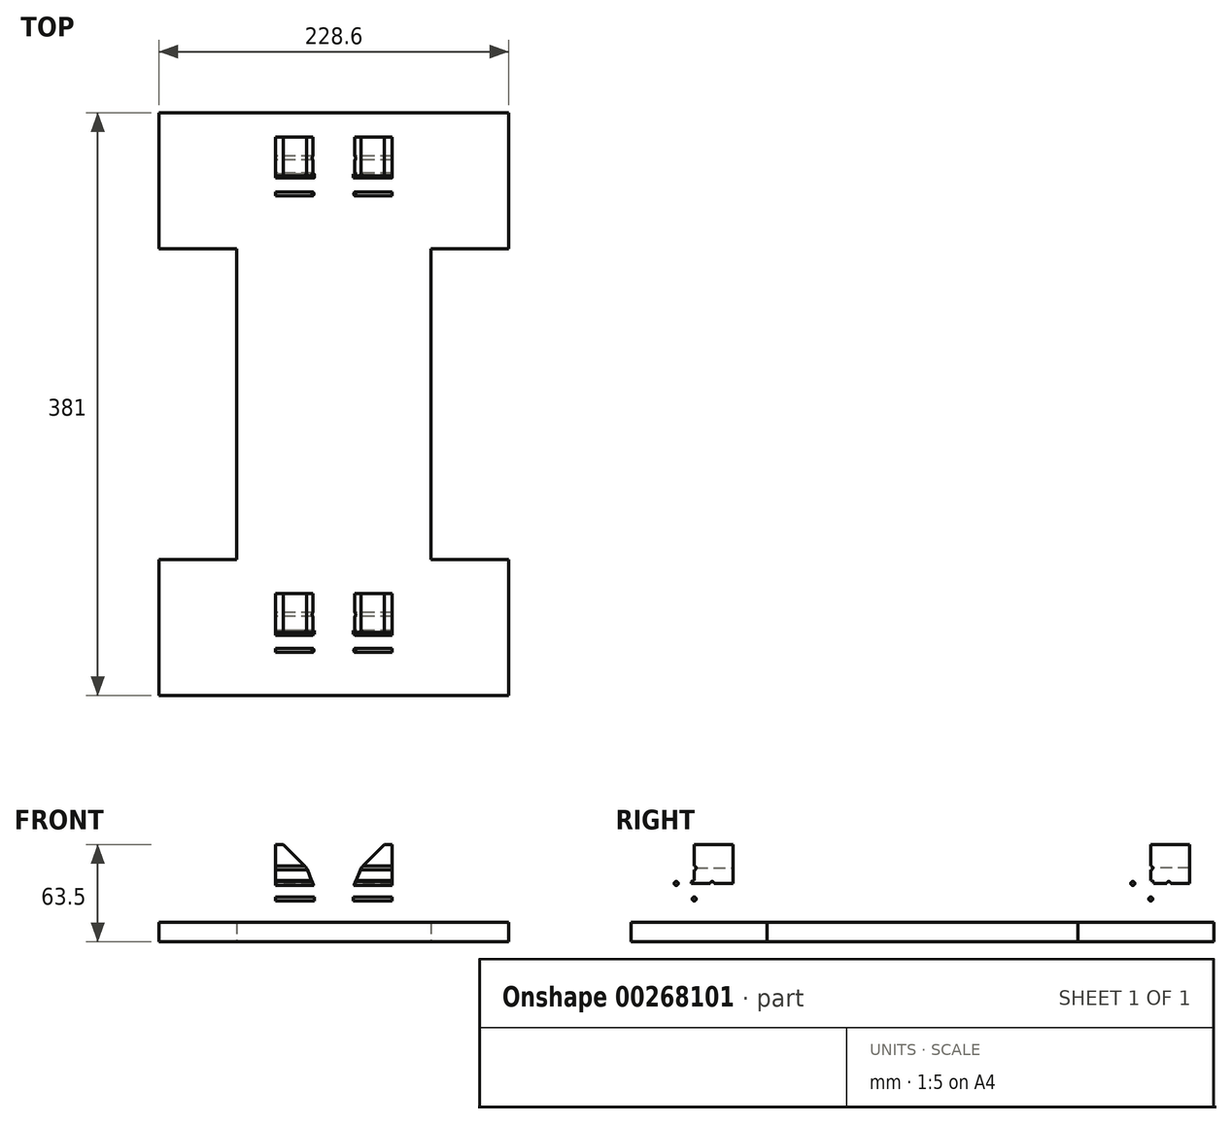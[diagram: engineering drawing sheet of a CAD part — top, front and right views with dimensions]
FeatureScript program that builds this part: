
annotation { "Feature Type Name" : "Feature", "Feature Type Description" : "" }
export const myFeature = defineFeature(function(context is Context, id is Id, definition is map)
    precondition{}
    {
        {
            var Q0;
            Q0=qCreatedBy(makeId("Top.planeOp"),FACE);
            var sketch = newSketch(context, id + "F0", { "sketchPlane" : qUnion([Q0])});
            skLineSegment(sketch, "E0.bottom", {"start": v(0, 0) * mm, "end": v(228.6, 0) * mm});
            skLineSegment(sketch, "E0.top", {"start": v(0, 381) * mm, "end": v(228.6, 381) * mm});
            skLineSegment(sketch, "E0.left", {"start": v(0, 0) * mm, "end": v(0, 381) * mm});
            skLineSegment(sketch, "E0.right", {"start": v(228.6, 0) * mm, "end": v(228.6, 381) * mm});
            skLineSegment(sketch, "E1", {"start": v(114.3, 381) * mm, "end": v(114.3, 0) * mm});
            skLineSegment(sketch, "E2", {"start": v(0, 190.5) * mm, "end": v(228.6, 190.5) * mm});
            skLineSegment(sketch, "E3.bottom", {"start": v(0, 190.5) * mm, "end": v(50.8, 190.5) * mm});
            skLineSegment(sketch, "E3.top", {"start": v(0, 88.9) * mm, "end": v(50.8, 88.9) * mm});
            skLineSegment(sketch, "E3.left", {"start": v(0, 190.5) * mm, "end": v(0, 88.9) * mm});
            skLineSegment(sketch, "E3.right", {"start": v(50.8, 190.5) * mm, "end": v(50.8, 88.9) * mm});
            skLineSegment(sketch, "E4.MirrorCS", {"start": v(50.8, 190.5) * mm, "end": v(50.8, 292.1) * mm});
            skLineSegment(sketch, "E5.MirrorCS", {"start": v(0, 292.1) * mm, "end": v(50.8, 292.1) * mm});
            skLineSegment(sketch, "E6.MirrorCS", {"start": v(177.8, 190.5) * mm, "end": v(177.8, 292.1) * mm});
            skLineSegment(sketch, "E7.MirrorCS", {"start": v(177.8, 190.5) * mm, "end": v(177.8, 88.9) * mm});
            skLineSegment(sketch, "E8.MirrorCS", {"start": v(228.6, 292.1) * mm, "end": v(177.8, 292.1) * mm});
            skLineSegment(sketch, "E9.MirrorCS", {"start": v(228.6, 88.9) * mm, "end": v(177.8, 88.9) * mm});
            skSolve(sketch);
        }
        {
            var Q0;
            {var subQ0=sQuery(id+"F0.wireOp",EDGE,"E4.MirrorCS");Q0=makeQuery(id+"F0.imprint","IMPRINT",FACE,{"disambiguationData":[TD([[makeQuery(id+"F0.imprint","IMPRINT",EDGE,{"derivedFrom":subQ0}),-1.0]])]});}
            var Q1;
            {var subQ0=sQuery(id+"F0.wireOp",EDGE,"E6.MirrorCS");Q1=makeQuery(id+"F0.imprint","IMPRINT",FACE,{"disambiguationData":[TD([[makeQuery(id+"F0.imprint","IMPRINT",EDGE,{"derivedFrom":subQ0}),1.0]])]});}
            var Q2;
            {var subQ4=sQuery(id+"F0.wireOp",EDGE,"E3.top");Q2=makeQuery(id+"F0.imprint","IMPRINT",FACE,{"disambiguationData":[TD([[makeQuery(id+"F0.imprint","IMPRINT",EDGE,{"derivedFrom":subQ4}),-1.0]])]});}
            var Q3;
            {var subQ0=sQuery(id+"F0.wireOp",EDGE,"E7.MirrorCS");Q3=makeQuery(id+"F0.imprint","IMPRINT",FACE,{"disambiguationData":[TD([[makeQuery(id+"F0.imprint","IMPRINT",EDGE,{"derivedFrom":subQ0}),-1.0]])]});}
            extrude(context, id + "F1", {"entities" : qUnion([Q0, Q1, Q2, Q3]), "depth" : 12.7 * mm});
        }
        {
            var Q0;
            Q0=qCreatedBy(makeId("Top.planeOp"),FACE);
            var sketch = newSketch(context, id + "F2", { "sketchPlane" : qUnion([Q0])});
            skLineSegment(sketch, "E10", {"start": v(0, 0) * mm, "end": v(0, 397.67) * mm});
            skLineSegment(sketch, "E11", {"start": v(0, 0) * mm, "end": v(531.22, 0) * mm});
            skLineSegment(sketch, "E12.bottom", {"start": v(76.2, 15.88) * mm, "end": v(101.6, 15.88) * mm});
            skLineSegment(sketch, "E12.top", {"start": v(76.2, 66.68) * mm, "end": v(101.6, 66.68) * mm});
            skLineSegment(sketch, "E12.left", {"start": v(76.2, 15.88) * mm, "end": v(76.2, 66.68) * mm});
            skLineSegment(sketch, "E12.right", {"start": v(101.6, 15.88) * mm, "end": v(101.6, 66.68) * mm});
            skLineSegment(sketch, "E13", {"start": v(0, 190.5) * mm, "end": v(186.8, 190.5) * mm});
            skLineSegment(sketch, "E14", {"start": v(114.3, 0) * mm, "end": v(114.3, 473.13) * mm});
            skLineSegment(sketch, "E15.MirrorCS", {"start": v(127, 15.88) * mm, "end": v(127, 66.68) * mm});
            skLineSegment(sketch, "E16.MirrorCS", {"start": v(152.4, 66.68) * mm, "end": v(127, 66.68) * mm});
            skLineSegment(sketch, "E17.MirrorCS", {"start": v(152.4, 15.88) * mm, "end": v(152.4, 66.68) * mm});
            skLineSegment(sketch, "E18.MirrorCS", {"start": v(152.4, 15.88) * mm, "end": v(127, 15.88) * mm});
            skLineSegment(sketch, "E19.MirrorCS", {"start": v(76.2, 314.33) * mm, "end": v(101.6, 314.33) * mm});
            skLineSegment(sketch, "E20.MirrorCS", {"start": v(76.2, 365.13) * mm, "end": v(76.2, 314.33) * mm});
            skLineSegment(sketch, "E21.MirrorCS", {"start": v(101.6, 365.13) * mm, "end": v(101.6, 314.33) * mm});
            skLineSegment(sketch, "E22.MirrorCS", {"start": v(76.2, 365.13) * mm, "end": v(101.6, 365.13) * mm});
            skLineSegment(sketch, "E23.MirrorCS", {"start": v(152.4, 314.33) * mm, "end": v(127, 314.33) * mm});
            skLineSegment(sketch, "E24.MirrorCS", {"start": v(127, 365.13) * mm, "end": v(127, 314.33) * mm});
            skLineSegment(sketch, "E25.MirrorCS", {"start": v(152.4, 365.13) * mm, "end": v(152.4, 314.33) * mm});
            skLineSegment(sketch, "E26.MirrorCS", {"start": v(152.4, 365.13) * mm, "end": v(127, 365.13) * mm});
            skSolve(sketch);
        }
        {
            var Q0;
            Q0=makeQuery(id+"F2.imprint","IMPRINT",FACE,{"disambiguationData":[TD([[makeQuery(id+"F2.imprint","IMPRINT",EDGE,{"derivedFrom":sQuery(id+"F2.wireOp",EDGE,"E23.MirrorCS")}),-1.0]])]});
            var Q1;
            Q1=makeQuery(id+"F2.imprint","IMPRINT",FACE,{"disambiguationData":[TD([[makeQuery(id+"F2.imprint","IMPRINT",EDGE,{"derivedFrom":sQuery(id+"F2.wireOp",EDGE,"E19.MirrorCS")}),1.0]])]});
            var Q2;
            Q2=makeQuery(id+"F2.imprint","IMPRINT",FACE,{"disambiguationData":[TD([[makeQuery(id+"F2.imprint","IMPRINT",EDGE,{"derivedFrom":sQuery(id+"F2.wireOp",EDGE,"E15.MirrorCS")}),-1.0]])]});
            var Q3;
            Q3=makeQuery(id+"F2.imprint","IMPRINT",FACE,{"disambiguationData":[TD([[makeQuery(id+"F2.imprint","IMPRINT",EDGE,{"derivedFrom":sQuery(id+"F2.wireOp",EDGE,"E12.bottom")}),1.0]])]});
            extrude(context, id + "F3", {"entities" : qUnion([Q0, Q1, Q2, Q3]), "operationType" : NewBodyOperationType.ADD, "depth" : 63.5 * mm});
        }
        {
            var Q0;
            Q0=makeQuery(id+"F3.opExtrude","CAP_EDGE",EDGE,{"disambiguationData":[OSD([sQuery(id+"F2.wireOp",EDGE,"E12.right")])],"isStart":false});
            var Q1;
            Q1=makeQuery(id+"F3.opExtrude","CAP_EDGE",EDGE,{"disambiguationData":[OSD([sQuery(id+"F2.wireOp",EDGE,"E15.MirrorCS")])],"isStart":false});
            var Q2;
            Q2=makeQuery(id+"F3.opExtrude","CAP_EDGE",EDGE,{"disambiguationData":[OSD([sQuery(id+"F2.wireOp",EDGE,"E24.MirrorCS")])],"isStart":false});
            var Q3;
            Q3=makeQuery(id+"F3.opExtrude","CAP_EDGE",EDGE,{"disambiguationData":[OSD([sQuery(id+"F2.wireOp",EDGE,"E21.MirrorCS")])],"isStart":false});
            chamfer(context, id + "F4", {"entities" : qUnion([Q0, Q1, Q2, Q3]), "width" : 20.32 * mm, "tangentPropagation" : true});
        }
        {
            var Q0;
            {var subQ0=sQuery(id+"F2.wireOp",EDGE,"E24.MirrorCS");Q0=makeQuery(id+"F4.opChamfer","BLEND_EDGE",EDGE,{"blendedFrom":[makeQuery(id+"F3.opExtrude","CAP_EDGE",EDGE,{"disambiguationData":[OSD([subQ0])],"isStart":false}),makeQuery(id+"F3.opExtrude","SWEPT_FACE",FACE,{"disambiguationData":[OSD([subQ0])]})],"blendedInto":[makeQuery(id+"F3.opExtrude","SWEPT_FACE",FACE,{"disambiguationData":[OSD([subQ0])]})]});}
            var Q1;
            {var subQ0=sQuery(id+"F2.wireOp",EDGE,"E21.MirrorCS");Q1=makeQuery(id+"F4.opChamfer","BLEND_EDGE",EDGE,{"blendedFrom":[makeQuery(id+"F3.opExtrude","CAP_EDGE",EDGE,{"disambiguationData":[OSD([subQ0])],"isStart":false}),makeQuery(id+"F3.opExtrude","SWEPT_FACE",FACE,{"disambiguationData":[OSD([subQ0])]})],"blendedInto":[makeQuery(id+"F3.opExtrude","SWEPT_FACE",FACE,{"disambiguationData":[OSD([subQ0])]})]});}
            var Q2;
            {var subQ0=sQuery(id+"F2.wireOp",EDGE,"E15.MirrorCS");Q2=makeQuery(id+"F4.opChamfer","BLEND_EDGE",EDGE,{"blendedFrom":[makeQuery(id+"F3.opExtrude","CAP_EDGE",EDGE,{"disambiguationData":[OSD([subQ0])],"isStart":false}),makeQuery(id+"F3.opExtrude","SWEPT_FACE",FACE,{"disambiguationData":[OSD([subQ0])]})],"blendedInto":[makeQuery(id+"F3.opExtrude","SWEPT_FACE",FACE,{"disambiguationData":[OSD([subQ0])]})]});}
            var Q3;
            {var subQ0=sQuery(id+"F2.wireOp",EDGE,"E12.right");Q3=makeQuery(id+"F4.opChamfer","BLEND_EDGE",EDGE,{"blendedFrom":[makeQuery(id+"F3.opExtrude","CAP_EDGE",EDGE,{"disambiguationData":[OSD([subQ0])],"isStart":false}),makeQuery(id+"F3.opExtrude","SWEPT_FACE",FACE,{"disambiguationData":[OSD([subQ0])]})],"blendedInto":[makeQuery(id+"F3.opExtrude","SWEPT_FACE",FACE,{"disambiguationData":[OSD([subQ0])]})]});}
            chamfer(context, id + "F5", {"entities" : qUnion([Q0, Q1, Q2, Q3]), "width" : 17.78 * mm, "tangentPropagation" : true});
        }
        {
            var Q0;
            Q0=makeQuery(id+"F3.opExtrude","SWEPT_FACE",FACE,{"disambiguationData":[OSD([sQuery(id+"F2.wireOp",EDGE,"E12.left")])]});
            var sketch = newSketch(context, id + "F6", { "sketchPlane" : qUnion([Q0])});
            skLineSegment(sketch, "E27.bottom", {"start": v(-66.67, 63.5) * mm, "end": v(-15.87, 63.5) * mm});
            skLineSegment(sketch, "E27.top", {"start": v(-66.67, 12.7) * mm, "end": v(-15.87, 12.7) * mm});
            skLineSegment(sketch, "E27.left", {"start": v(-66.67, 63.5) * mm, "end": v(-66.67, 12.7) * mm});
            skLineSegment(sketch, "E27.right", {"start": v(-15.87, 63.5) * mm, "end": v(-15.87, 12.7) * mm});
            skCircle(sketch, "E28", {"center": v(-41.27, 38.1) * mm, "radius": 2.03 * mm});
            skLineSegment(sketch, "E29", {"start": v(-41.27, 63.5) * mm, "end": v(-41.27, 12.7) * mm});
            skLineSegment(sketch, "E30", {"start": v(-66.67, 38.1) * mm, "end": v(-15.87, 38.1) * mm});
            skCircle(sketch, "E31", {"center": v(-53.02, 38.1) * mm, "radius": 1.27 * mm});
            skCircle(sketch, "E32", {"center": v(-41.27, 28) * mm, "radius": 1.27 * mm});
            skCircle(sketch, "E33.MirrorC", {"center": v(-29.53, 38.1) * mm, "radius": 1.27 * mm});
            skCircle(sketch, "E34.MirrorC", {"center": v(-41.27, 48.2) * mm, "radius": 1.27 * mm});
            skSolve(sketch);
        }
        {
            var Q0;
            {var subQ0=sQuery(id+"F6.wireOp",EDGE,"E34.MirrorC");var subQ1=sQuery(id+"F6.wireOp",EDGE,"E29");var subQ2=makeQuery(id+"F6.imprint","INTERSECT",VERTEX,{"disambiguationData":[OD(0.0)],"derivedFrom":[subQ1,subQ0]});Q0=makeQuery(id+"F6.imprint","IMPRINT",FACE,{"disambiguationData":[TD([[makeQuery(id+"F6.imprint","IMPRINT",EDGE,{"disambiguationData":[TD([[subQ2,-1.0]])],"derivedFrom":subQ1}),1.0]])]});}
            var Q1;
            {var subQ0=sQuery(id+"F6.wireOp",EDGE,"E34.MirrorC");var subQ1=sQuery(id+"F6.wireOp",EDGE,"E29");var subQ2=makeQuery(id+"F6.imprint","INTERSECT",VERTEX,{"disambiguationData":[OD(0.0)],"derivedFrom":[subQ1,subQ0]});Q1=makeQuery(id+"F6.imprint","IMPRINT",FACE,{"disambiguationData":[TD([[makeQuery(id+"F6.imprint","IMPRINT",EDGE,{"disambiguationData":[TD([[subQ2,-1.0]])],"derivedFrom":subQ1}),-1.0]])]});}
            var Q2;
            {var subQ0=sQuery(id+"F6.wireOp",EDGE,"E31");var subQ1=sQuery(id+"F6.wireOp",EDGE,"E30");var subQ2=makeQuery(id+"F6.imprint","INTERSECT",VERTEX,{"disambiguationData":[OD(0.0)],"derivedFrom":[subQ1,subQ0]});Q2=makeQuery(id+"F6.imprint","IMPRINT",FACE,{"disambiguationData":[TD([[makeQuery(id+"F6.imprint","IMPRINT",EDGE,{"disambiguationData":[TD([[subQ2,-1.0]])],"derivedFrom":subQ1}),1.0]])]});}
            var Q3;
            {var subQ0=sQuery(id+"F6.wireOp",EDGE,"E31");var subQ1=sQuery(id+"F6.wireOp",EDGE,"E30");var subQ2=makeQuery(id+"F6.imprint","INTERSECT",VERTEX,{"disambiguationData":[OD(0.0)],"derivedFrom":[subQ1,subQ0]});Q3=makeQuery(id+"F6.imprint","IMPRINT",FACE,{"disambiguationData":[TD([[makeQuery(id+"F6.imprint","IMPRINT",EDGE,{"disambiguationData":[TD([[subQ2,-1.0]])],"derivedFrom":subQ1}),-1.0]])]});}
            var Q4;
            {var subQ0=sQuery(id+"F6.wireOp",EDGE,"E29");var subQ1=sQuery(id+"F6.wireOp",EDGE,"E28");var subQ2=makeQuery(id+"F6.imprint","INTERSECT",VERTEX,{"disambiguationData":[OD(0.0)],"derivedFrom":[subQ1,subQ0]});Q4=makeQuery(id+"F6.imprint","IMPRINT",FACE,{"disambiguationData":[TD([[makeQuery(id+"F6.imprint","IMPRINT",EDGE,{"disambiguationData":[TD([[subQ2,1.0]])],"derivedFrom":subQ1}),1.0]])]});}
            var Q5;
            {var subQ0=sQuery(id+"F6.wireOp",EDGE,"E29");var subQ1=sQuery(id+"F6.wireOp",EDGE,"E28");var subQ2=makeQuery(id+"F6.imprint","INTERSECT",VERTEX,{"disambiguationData":[OD(0.0)],"derivedFrom":[subQ1,subQ0]});Q5=makeQuery(id+"F6.imprint","IMPRINT",FACE,{"disambiguationData":[TD([[makeQuery(id+"F6.imprint","IMPRINT",EDGE,{"disambiguationData":[TD([[subQ2,-1.0]])],"derivedFrom":subQ1}),1.0]])]});}
            var Q6;
            {var subQ0=sQuery(id+"F6.wireOp",EDGE,"E30");var subQ1=sQuery(id+"F6.wireOp",EDGE,"E28");var subQ2=makeQuery(id+"F6.imprint","INTERSECT",VERTEX,{"disambiguationData":[OD(1.0)],"derivedFrom":[subQ1,subQ0]});Q6=makeQuery(id+"F6.imprint","IMPRINT",FACE,{"disambiguationData":[TD([[makeQuery(id+"F6.imprint","IMPRINT",EDGE,{"disambiguationData":[TD([[subQ2,-1.0]])],"derivedFrom":subQ1}),1.0]])]});}
            var Q7;
            {var subQ0=sQuery(id+"F6.wireOp",EDGE,"E32");var subQ1=sQuery(id+"F6.wireOp",EDGE,"E29");var subQ2=makeQuery(id+"F6.imprint","INTERSECT",VERTEX,{"disambiguationData":[OD(0.0)],"derivedFrom":[subQ1,subQ0]});Q7=makeQuery(id+"F6.imprint","IMPRINT",FACE,{"disambiguationData":[TD([[makeQuery(id+"F6.imprint","IMPRINT",EDGE,{"disambiguationData":[TD([[subQ2,-1.0]])],"derivedFrom":subQ1}),-1.0]])]});}
            var Q8;
            {var subQ0=sQuery(id+"F6.wireOp",EDGE,"E32");var subQ1=sQuery(id+"F6.wireOp",EDGE,"E29");var subQ2=makeQuery(id+"F6.imprint","INTERSECT",VERTEX,{"disambiguationData":[OD(0.0)],"derivedFrom":[subQ1,subQ0]});Q8=makeQuery(id+"F6.imprint","IMPRINT",FACE,{"disambiguationData":[TD([[makeQuery(id+"F6.imprint","IMPRINT",EDGE,{"disambiguationData":[TD([[subQ2,-1.0]])],"derivedFrom":subQ1}),1.0]])]});}
            var Q9;
            {var subQ0=sQuery(id+"F6.wireOp",EDGE,"E33.MirrorC");var subQ1=sQuery(id+"F6.wireOp",EDGE,"E30");var subQ2=makeQuery(id+"F6.imprint","INTERSECT",VERTEX,{"disambiguationData":[OD(0.0)],"derivedFrom":[subQ1,subQ0]});Q9=makeQuery(id+"F6.imprint","IMPRINT",FACE,{"disambiguationData":[TD([[makeQuery(id+"F6.imprint","IMPRINT",EDGE,{"disambiguationData":[TD([[subQ2,-1.0]])],"derivedFrom":subQ1}),1.0]])]});}
            var Q10;
            {var subQ0=sQuery(id+"F6.wireOp",EDGE,"E33.MirrorC");var subQ1=sQuery(id+"F6.wireOp",EDGE,"E30");var subQ2=makeQuery(id+"F6.imprint","INTERSECT",VERTEX,{"disambiguationData":[OD(0.0)],"derivedFrom":[subQ1,subQ0]});Q10=makeQuery(id+"F6.imprint","IMPRINT",FACE,{"disambiguationData":[TD([[makeQuery(id+"F6.imprint","IMPRINT",EDGE,{"disambiguationData":[TD([[subQ2,-1.0]])],"derivedFrom":subQ1}),-1.0]])]});}
            var Q11;
            {var subQ0=sQuery(id+"F6.wireOp",EDGE,"E30");var subQ1=sQuery(id+"F6.wireOp",EDGE,"E28");var subQ2=makeQuery(id+"F6.imprint","INTERSECT",VERTEX,{"disambiguationData":[OD(0.0)],"derivedFrom":[subQ1,subQ0]});Q11=makeQuery(id+"F6.imprint","IMPRINT",FACE,{"disambiguationData":[TD([[makeQuery(id+"F6.imprint","IMPRINT",EDGE,{"disambiguationData":[TD([[subQ2,1.0]])],"derivedFrom":subQ1}),1.0]])]});}
            extrude(context, id + "F7", {"entities" : qUnion([Q0, Q1, Q2, Q3, Q4, Q5, Q6, Q7, Q8, Q9, Q10, Q11]), "operationType" : NewBodyOperationType.REMOVE, "oppositeDirection" : true, "depth" : 254 * mm});
        }
        {
            var Q0;
            Q0=makeQuery(id+"F3.opExtrude","SWEPT_FACE",FACE,{"disambiguationData":[OSD([sQuery(id+"F2.wireOp",EDGE,"E20.MirrorCS")])]});
            var sketch = newSketch(context, id + "F8", { "sketchPlane" : qUnion([Q0])});
            skLineSegment(sketch, "E35.bottom", {"start": v(-365.13, 63.5) * mm, "end": v(-314.33, 63.5) * mm});
            skLineSegment(sketch, "E35.top", {"start": v(-365.13, 12.7) * mm, "end": v(-314.33, 12.7) * mm});
            skLineSegment(sketch, "E35.left", {"start": v(-365.13, 63.5) * mm, "end": v(-365.13, 12.7) * mm});
            skLineSegment(sketch, "E35.right", {"start": v(-314.33, 63.5) * mm, "end": v(-314.33, 12.7) * mm});
            skCircle(sketch, "E36", {"center": v(-339.73, 38.1) * mm, "radius": 2.03 * mm});
            skLineSegment(sketch, "E37", {"start": v(-339.73, 63.5) * mm, "end": v(-339.73, 12.7) * mm});
            skLineSegment(sketch, "E38", {"start": v(-365.13, 38.1) * mm, "end": v(-314.33, 38.1) * mm});
            skCircle(sketch, "E39", {"center": v(-351.47, 38.1) * mm, "radius": 1.27 * mm});
            skCircle(sketch, "E40", {"center": v(-339.73, 28) * mm, "radius": 1.27 * mm});
            skCircle(sketch, "E41.MirrorC", {"center": v(-327.98, 38.1) * mm, "radius": 1.27 * mm});
            skCircle(sketch, "E42.MirrorC", {"center": v(-339.73, 48.2) * mm, "radius": 1.27 * mm});
            skSolve(sketch);
        }
        {
            var Q0;
            {var subQ0=sQuery(id+"F8.wireOp",EDGE,"E42.MirrorC");var subQ1=sQuery(id+"F8.wireOp",EDGE,"E37");var subQ2=makeQuery(id+"F8.imprint","INTERSECT",VERTEX,{"disambiguationData":[OD(0.0)],"derivedFrom":[subQ1,subQ0]});Q0=makeQuery(id+"F8.imprint","IMPRINT",FACE,{"disambiguationData":[TD([[makeQuery(id+"F8.imprint","IMPRINT",EDGE,{"disambiguationData":[TD([[subQ2,-1.0]])],"derivedFrom":subQ1}),1.0]])]});}
            var Q1;
            {var subQ0=sQuery(id+"F8.wireOp",EDGE,"E42.MirrorC");var subQ1=sQuery(id+"F8.wireOp",EDGE,"E37");var subQ2=makeQuery(id+"F8.imprint","INTERSECT",VERTEX,{"disambiguationData":[OD(0.0)],"derivedFrom":[subQ1,subQ0]});Q1=makeQuery(id+"F8.imprint","IMPRINT",FACE,{"disambiguationData":[TD([[makeQuery(id+"F8.imprint","IMPRINT",EDGE,{"disambiguationData":[TD([[subQ2,-1.0]])],"derivedFrom":subQ1}),-1.0]])]});}
            var Q2;
            {var subQ0=sQuery(id+"F8.wireOp",EDGE,"E39");var subQ1=sQuery(id+"F8.wireOp",EDGE,"E38");var subQ2=makeQuery(id+"F8.imprint","INTERSECT",VERTEX,{"disambiguationData":[OD(0.0)],"derivedFrom":[subQ1,subQ0]});Q2=makeQuery(id+"F8.imprint","IMPRINT",FACE,{"disambiguationData":[TD([[makeQuery(id+"F8.imprint","IMPRINT",EDGE,{"disambiguationData":[TD([[subQ2,-1.0]])],"derivedFrom":subQ1}),-1.0]])]});}
            var Q3;
            {var subQ0=sQuery(id+"F8.wireOp",EDGE,"E39");var subQ1=sQuery(id+"F8.wireOp",EDGE,"E38");var subQ2=makeQuery(id+"F8.imprint","INTERSECT",VERTEX,{"disambiguationData":[OD(0.0)],"derivedFrom":[subQ1,subQ0]});Q3=makeQuery(id+"F8.imprint","IMPRINT",FACE,{"disambiguationData":[TD([[makeQuery(id+"F8.imprint","IMPRINT",EDGE,{"disambiguationData":[TD([[subQ2,-1.0]])],"derivedFrom":subQ1}),1.0]])]});}
            var Q4;
            {var subQ0=sQuery(id+"F8.wireOp",EDGE,"E37");var subQ1=sQuery(id+"F8.wireOp",EDGE,"E36");var subQ2=makeQuery(id+"F8.imprint","INTERSECT",VERTEX,{"disambiguationData":[OD(0.0)],"derivedFrom":[subQ1,subQ0]});Q4=makeQuery(id+"F8.imprint","IMPRINT",FACE,{"disambiguationData":[TD([[makeQuery(id+"F8.imprint","IMPRINT",EDGE,{"disambiguationData":[TD([[subQ2,-1.0]])],"derivedFrom":subQ1}),1.0]])]});}
            var Q5;
            {var subQ0=sQuery(id+"F8.wireOp",EDGE,"E38");var subQ1=sQuery(id+"F8.wireOp",EDGE,"E36");var subQ2=makeQuery(id+"F8.imprint","INTERSECT",VERTEX,{"disambiguationData":[OD(0.0)],"derivedFrom":[subQ1,subQ0]});Q5=makeQuery(id+"F8.imprint","IMPRINT",FACE,{"disambiguationData":[TD([[makeQuery(id+"F8.imprint","IMPRINT",EDGE,{"disambiguationData":[TD([[subQ2,1.0]])],"derivedFrom":subQ1}),1.0]])]});}
            var Q6;
            {var subQ0=sQuery(id+"F8.wireOp",EDGE,"E37");var subQ1=sQuery(id+"F8.wireOp",EDGE,"E36");var subQ2=makeQuery(id+"F8.imprint","INTERSECT",VERTEX,{"disambiguationData":[OD(0.0)],"derivedFrom":[subQ1,subQ0]});Q6=makeQuery(id+"F8.imprint","IMPRINT",FACE,{"disambiguationData":[TD([[makeQuery(id+"F8.imprint","IMPRINT",EDGE,{"disambiguationData":[TD([[subQ2,1.0]])],"derivedFrom":subQ1}),1.0]])]});}
            var Q7;
            {var subQ0=sQuery(id+"F8.wireOp",EDGE,"E38");var subQ1=sQuery(id+"F8.wireOp",EDGE,"E36");var subQ2=makeQuery(id+"F8.imprint","INTERSECT",VERTEX,{"disambiguationData":[OD(1.0)],"derivedFrom":[subQ1,subQ0]});Q7=makeQuery(id+"F8.imprint","IMPRINT",FACE,{"disambiguationData":[TD([[makeQuery(id+"F8.imprint","IMPRINT",EDGE,{"disambiguationData":[TD([[subQ2,-1.0]])],"derivedFrom":subQ1}),1.0]])]});}
            var Q8;
            {var subQ0=sQuery(id+"F8.wireOp",EDGE,"E41.MirrorC");var subQ1=sQuery(id+"F8.wireOp",EDGE,"E38");var subQ2=makeQuery(id+"F8.imprint","INTERSECT",VERTEX,{"disambiguationData":[OD(0.0)],"derivedFrom":[subQ1,subQ0]});Q8=makeQuery(id+"F8.imprint","IMPRINT",FACE,{"disambiguationData":[TD([[makeQuery(id+"F8.imprint","IMPRINT",EDGE,{"disambiguationData":[TD([[subQ2,-1.0]])],"derivedFrom":subQ1}),1.0]])]});}
            var Q9;
            {var subQ0=sQuery(id+"F8.wireOp",EDGE,"E41.MirrorC");var subQ1=sQuery(id+"F8.wireOp",EDGE,"E38");var subQ2=makeQuery(id+"F8.imprint","INTERSECT",VERTEX,{"disambiguationData":[OD(0.0)],"derivedFrom":[subQ1,subQ0]});Q9=makeQuery(id+"F8.imprint","IMPRINT",FACE,{"disambiguationData":[TD([[makeQuery(id+"F8.imprint","IMPRINT",EDGE,{"disambiguationData":[TD([[subQ2,-1.0]])],"derivedFrom":subQ1}),-1.0]])]});}
            var Q10;
            {var subQ0=sQuery(id+"F8.wireOp",EDGE,"E40");var subQ1=sQuery(id+"F8.wireOp",EDGE,"E37");var subQ2=makeQuery(id+"F8.imprint","INTERSECT",VERTEX,{"disambiguationData":[OD(0.0)],"derivedFrom":[subQ1,subQ0]});Q10=makeQuery(id+"F8.imprint","IMPRINT",FACE,{"disambiguationData":[TD([[makeQuery(id+"F8.imprint","IMPRINT",EDGE,{"disambiguationData":[TD([[subQ2,-1.0]])],"derivedFrom":subQ1}),1.0]])]});}
            var Q11;
            {var subQ0=sQuery(id+"F8.wireOp",EDGE,"E40");var subQ1=sQuery(id+"F8.wireOp",EDGE,"E37");var subQ2=makeQuery(id+"F8.imprint","INTERSECT",VERTEX,{"disambiguationData":[OD(0.0)],"derivedFrom":[subQ1,subQ0]});Q11=makeQuery(id+"F8.imprint","IMPRINT",FACE,{"disambiguationData":[TD([[makeQuery(id+"F8.imprint","IMPRINT",EDGE,{"disambiguationData":[TD([[subQ2,-1.0]])],"derivedFrom":subQ1}),-1.0]])]});}
            extrude(context, id + "F9", {"entities" : qUnion([Q0, Q1, Q2, Q3, Q4, Q5, Q6, Q7, Q8, Q9, Q10, Q11]), "operationType" : NewBodyOperationType.REMOVE, "oppositeDirection" : true, "depth" : 254 * mm});
        }
    });
